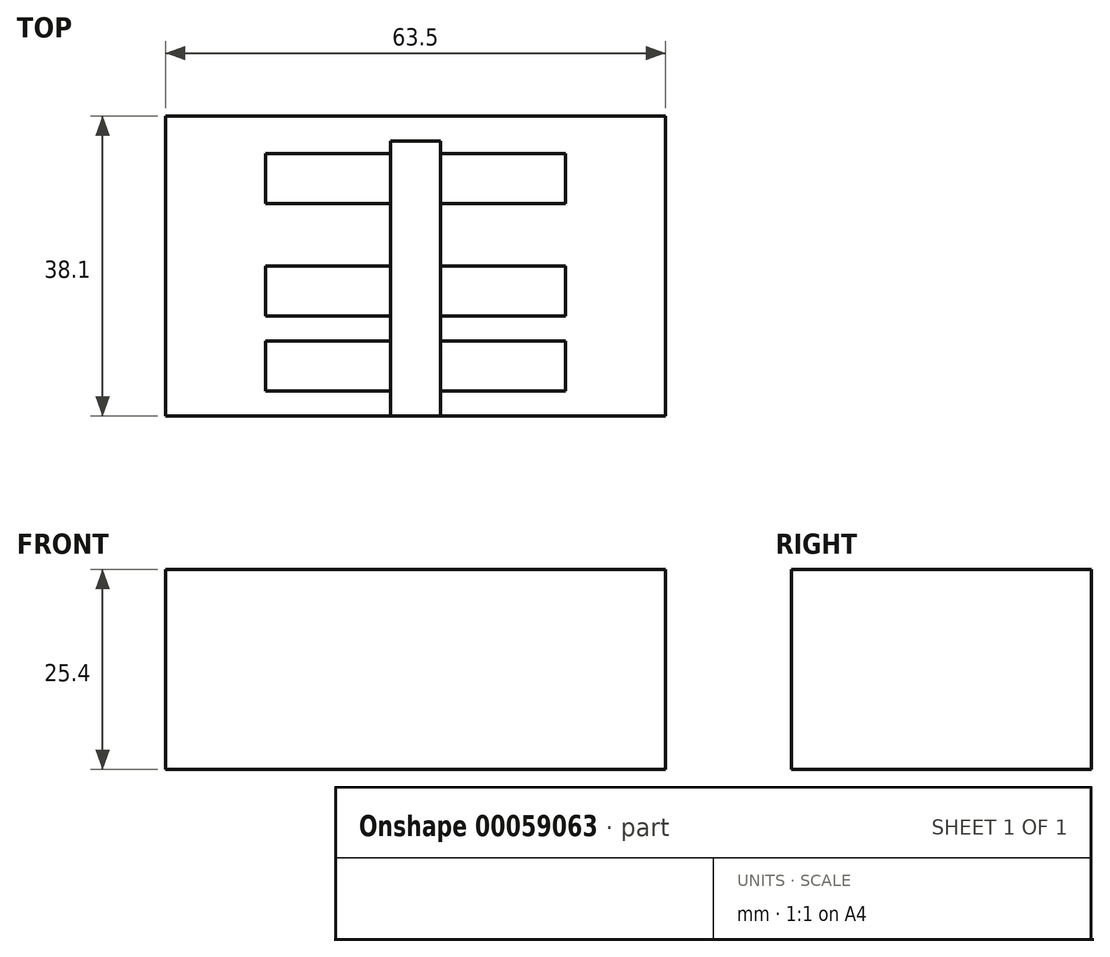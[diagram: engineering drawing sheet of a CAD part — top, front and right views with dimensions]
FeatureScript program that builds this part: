
annotation { "Feature Type Name" : "Feature", "Feature Type Description" : "" }
export const myFeature = defineFeature(function(context is Context, id is Id, definition is map)
    precondition{}
    {
        {
            var Q0;
            Q0=qCreatedBy(makeId("Top.planeOp"),FACE);
            var sketch = newSketch(context, id + "F0", { "sketchPlane" : qUnion([Q0])});
            skLineSegment(sketch, "E0.bottom", {"start": v(31.75, -19.05) * mm, "end": v(-31.75, -19.05) * mm});
            skLineSegment(sketch, "E0.top", {"start": v(31.75, 19.05) * mm, "end": v(-31.75, 19.05) * mm});
            skLineSegment(sketch, "E0.left", {"start": v(31.75, -19.05) * mm, "end": v(31.75, 19.05) * mm});
            skLineSegment(sketch, "E0.right", {"start": v(-31.75, -19.05) * mm, "end": v(-31.75, 19.05) * mm});
            skPoint(sketch, "E0.middle", {"position": v(0, 0) * mm});
            skSolve(sketch);
        }
        {
            var Q0;
            Q0 = qSketchRegion(id + "F0", true);
            extrude(context, id + "F1", {"entities" : qUnion([Q0]), "depth" : 25.4 * mm});
        }
        {
            var Q0;
            Q0=makeQuery(id+"F1.opExtrude","CAP_FACE",FACE,{"disambiguationData":[OSD([sQuery(id+"F0.wireOp",EDGE,"E0.bottom"),sQuery(id+"F0.wireOp",EDGE,"E0.top"),sQuery(id+"F0.wireOp",EDGE,"E0.left"),sQuery(id+"F0.wireOp",EDGE,"E0.right")])],"isStart":false});
            var sketch = newSketch(context, id + "F2", { "sketchPlane" : qUnion([Q0])});
            skLineSegment(sketch, "E1", {"start": v(-3.17, -19.05) * mm, "end": v(-3.17, 15.88) * mm});
            skLineSegment(sketch, "E2", {"start": v(-3.17, 15.88) * mm, "end": v(3.17, 15.88) * mm});
            skLineSegment(sketch, "E3", {"start": v(3.17, 15.88) * mm, "end": v(3.18, -19.05) * mm});
            skLineSegment(sketch, "E4", {"start": v(3.17, 0) * mm, "end": v(-3.17, 0) * mm, "construction": true});
            skLineSegment(sketch, "E5", {"start": v(-3.17, -19.05) * mm, "end": v(3.17, -19.05) * mm});
            skSolve(sketch);
        }
        {
            var Q0;
            {var subQ14=sQuery(id+"F2.wireOp",EDGE,"E2");Q0=makeQuery(id+"F2.imprint","IMPRINT",FACE,{"disambiguationData":[TD([[makeQuery(id+"F2.imprint","IMPRINT",EDGE,{"derivedFrom":subQ14}),1.0]])]});}
            var sketch = newSketch(context, id + "F3", { "sketchPlane" : qUnion([Q0])});
            skLineSegment(sketch, "E6.bottom", {"start": v(-19.05, 14.29) * mm, "end": v(19.05, 14.29) * mm});
            skLineSegment(sketch, "E6.top", {"start": v(-19.05, 7.94) * mm, "end": v(19.05, 7.94) * mm});
            skLineSegment(sketch, "E6.left", {"start": v(-19.05, 14.29) * mm, "end": v(-19.05, 7.94) * mm});
            skLineSegment(sketch, "E6.right", {"start": v(19.05, 14.29) * mm, "end": v(19.05, 7.94) * mm});
            skLineSegment(sketch, "E7.bottom", {"start": v(-19.05, -9.52) * mm, "end": v(19.05, -9.52) * mm});
            skLineSegment(sketch, "E7.top", {"start": v(-19.05, -15.87) * mm, "end": v(19.05, -15.87) * mm});
            skLineSegment(sketch, "E7.left", {"start": v(-19.05, -9.52) * mm, "end": v(-19.05, -15.88) * mm});
            skLineSegment(sketch, "E7.right", {"start": v(19.05, -9.52) * mm, "end": v(19.05, -15.87) * mm});
            skLineSegment(sketch, "E8.bottom", {"start": v(-19.05, 0) * mm, "end": v(19.05, 0) * mm});
            skLineSegment(sketch, "E8.top", {"start": v(-19.05, -6.35) * mm, "end": v(19.05, -6.35) * mm});
            skLineSegment(sketch, "E8.left", {"start": v(-19.05, 0) * mm, "end": v(-19.05, -6.35) * mm});
            skLineSegment(sketch, "E8.right", {"start": v(19.05, 0) * mm, "end": v(19.05, -6.35) * mm});
            skLineSegment(sketch, "E9", {"start": v(0, 35.3) * mm, "end": v(0, -26.4) * mm, "construction": true});
            skLineSegment(sketch, "E10", {"start": v(-19.05, 11.11) * mm, "end": v(0, 11.11) * mm, "construction": true});
            skLineSegment(sketch, "E11", {"start": v(0, 11.11) * mm, "end": v(19.05, 11.11) * mm, "construction": true});
            skLineSegment(sketch, "E12", {"start": v(-19.05, -3.18) * mm, "end": v(19.05, -3.17) * mm, "construction": true});
            skSolve(sketch);
        }
        {
            var Q0;
            Q0 = qSketchRegion(id + "F2", true);
            extrude(context, id + "F4", {"entities" : qUnion([Q0]), "operationType" : NewBodyOperationType.REMOVE, "oppositeDirection" : true, "depth" : 5 / 406.4 * mm});
        }
        {
            var Q0;
            {var subQ0=sQuery(id+"F3.wireOp",EDGE,"E6.right");Q0=makeQuery(id+"F3.imprint","IMPRINT",FACE,{"disambiguationData":[TD([[makeQuery(id+"F3.imprint","IMPRINT",EDGE,{"derivedFrom":subQ0}),-1.0]])]});}
            var Q1;
            {var subQ0=sQuery(id+"F3.wireOp",EDGE,"E6.left");Q1=makeQuery(id+"F3.imprint","IMPRINT",FACE,{"disambiguationData":[TD([[makeQuery(id+"F3.imprint","IMPRINT",EDGE,{"derivedFrom":subQ0}),1.0]])]});}
            var Q2;
            {var subQ0=sQuery(id+"F3.wireOp",EDGE,"E7.right");Q2=makeQuery(id+"F3.imprint","IMPRINT",FACE,{"disambiguationData":[TD([[makeQuery(id+"F3.imprint","IMPRINT",EDGE,{"derivedFrom":subQ0}),-1.0]])]});}
            var Q3;
            {var subQ0=sQuery(id+"F3.wireOp",EDGE,"E7.left");Q3=makeQuery(id+"F3.imprint","IMPRINT",FACE,{"disambiguationData":[TD([[makeQuery(id+"F3.imprint","IMPRINT",EDGE,{"derivedFrom":subQ0}),1.0]])]});}
            extrude(context, id + "F5", {"entities" : qUnion([Q0, Q1, Q2, Q3]), "operationType" : NewBodyOperationType.REMOVE, "oppositeDirection" : true, "depth" : 1 / 101.6 * mm});
        }
        {
            var Q0;
            {var subQ0=sQuery(id+"F3.wireOp",EDGE,"E8.right");Q0=makeQuery(id+"F3.imprint","IMPRINT",FACE,{"disambiguationData":[TD([[makeQuery(id+"F3.imprint","IMPRINT",EDGE,{"derivedFrom":subQ0}),-1.0]])]});}
            var Q1;
            {var subQ0=sQuery(id+"F3.wireOp",EDGE,"E8.left");Q1=makeQuery(id+"F3.imprint","IMPRINT",FACE,{"disambiguationData":[TD([[makeQuery(id+"F3.imprint","IMPRINT",EDGE,{"derivedFrom":subQ0}),1.0]])]});}
            extrude(context, id + "F6", {"entities" : qUnion([Q0, Q1]), "operationType" : NewBodyOperationType.REMOVE, "oppositeDirection" : true, "depth" : 3 / 406.4 * mm});
        }
    });
